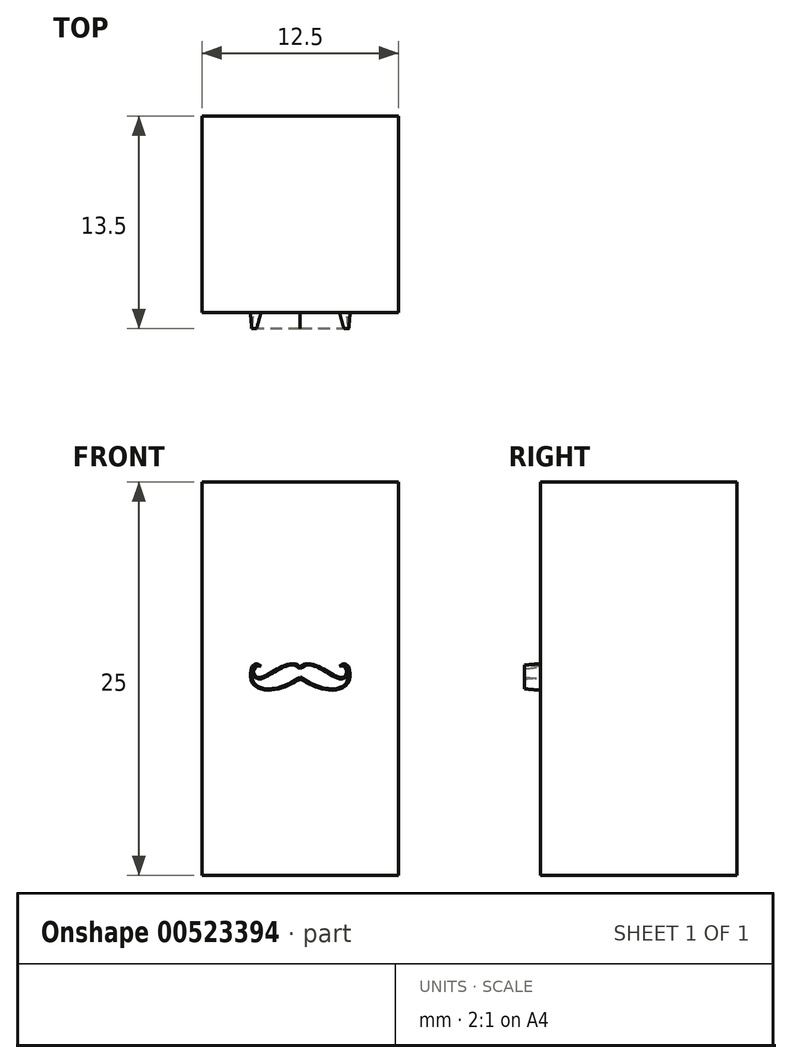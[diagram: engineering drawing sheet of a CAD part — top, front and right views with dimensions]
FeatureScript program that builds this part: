
annotation { "Feature Type Name" : "Feature", "Feature Type Description" : "" }
export const myFeature = defineFeature(function(context is Context, id is Id, definition is map)
    precondition{}
    {
        {
            var Q0;
            Q0=qCreatedBy(makeId("Top.planeOp"),FACE);
            var sketch = newSketch(context, id + "F0", { "sketchPlane" : qUnion([Q0])});
            skLineSegment(sketch, "E0.bottom", {"start": v(0, 0) * mm, "end": v(12.5, 0) * mm});
            skLineSegment(sketch, "E0.top", {"start": v(0, 12.5) * mm, "end": v(12.5, 12.5) * mm});
            skLineSegment(sketch, "E0.left", {"start": v(0, 0) * mm, "end": v(0, 12.5) * mm});
            skLineSegment(sketch, "E0.right", {"start": v(12.5, 0) * mm, "end": v(12.5, 12.5) * mm});
            skSolve(sketch);
        }
        {
            var Q0;
            Q0=makeQuery(id+"F0.imprint","IMPRINT",FACE,{"disambiguationData":[TD([[makeQuery(id+"F0.imprint","IMPRINT",EDGE,{"derivedFrom":sQuery(id+"F0.wireOp",EDGE,"E0.bottom")}),1.0]])]});
            extrude(context, id + "F1", {"entities" : qUnion([Q0]), "depth" : 25 * mm, "offsetDistance" : 25.4 * mm});
        }
        {
            var Q0;
            Q0=makeQuery(id+"F1.opExtrude","SWEPT_FACE",FACE,{"disambiguationData":[OSD([sQuery(id+"F0.wireOp",EDGE,"E0.bottom")])]});
            var sketch = newSketch(context, id + "F2", { "sketchPlane" : qUnion([Q0])});
            skFitSpline(sketch, "E1", {"points": [v(6.21, 12.53) * mm, v(9.39, 12.5) * mm, v(8.75, 13.3) * mm], "startDerivative": vector(7.27, -4.98) * mm, "endDerivative": vector(-4.08, -4.08) * mm});
            skFitSpline(sketch, "E2", {"points": [v(8.72, 13.3) * mm, v(9, 12.6) * mm, v(6.24, 13.24) * mm], "startDerivative": vector(5.5, 1.16) * mm, "endDerivative": vector(-3.68, -3.68) * mm});
            skLineSegment(sketch, "E3", {"start": v(6.25, 13.25) * mm, "end": v(6.25, 12.5) * mm, "construction": true});
            skLineSegment(sketch, "E4", {"start": v(6.25, 25) * mm, "end": v(6.25, 0) * mm, "construction": true});
            skPoint(sketch, "E5", {"position": v(6.25, 12.5) * mm});
            skFitSpline(sketch, "E6.MirrorCS", {"points": [v(6.29, 12.53) * mm, v(3.11, 12.5) * mm, v(3.75, 13.3) * mm], "startDerivative": vector(-7.27, -4.98) * mm, "endDerivative": vector(4.08, -4.08) * mm});
            skFitSpline(sketch, "E7.MirrorCS", {"points": [v(3.78, 13.3) * mm, v(3.5, 12.6) * mm, v(6.26, 13.24) * mm], "startDerivative": vector(-5.5, 1.16) * mm, "endDerivative": vector(3.68, -3.68) * mm});
            skSolve(sketch);
        }
        {
            var Q0;
            Q0 = qSketchRegion(id + "F2", true);
            extrude(context, id + "F3", {"entities" : qUnion([Q0]), "operationType" : NewBodyOperationType.ADD, "depth" : 1 * mm, "offsetDistance" : 25 * mm, "hasDraft" : true, "draftAngle" : 5 * degree, "draftPullDirection" : true});
        }
    });
